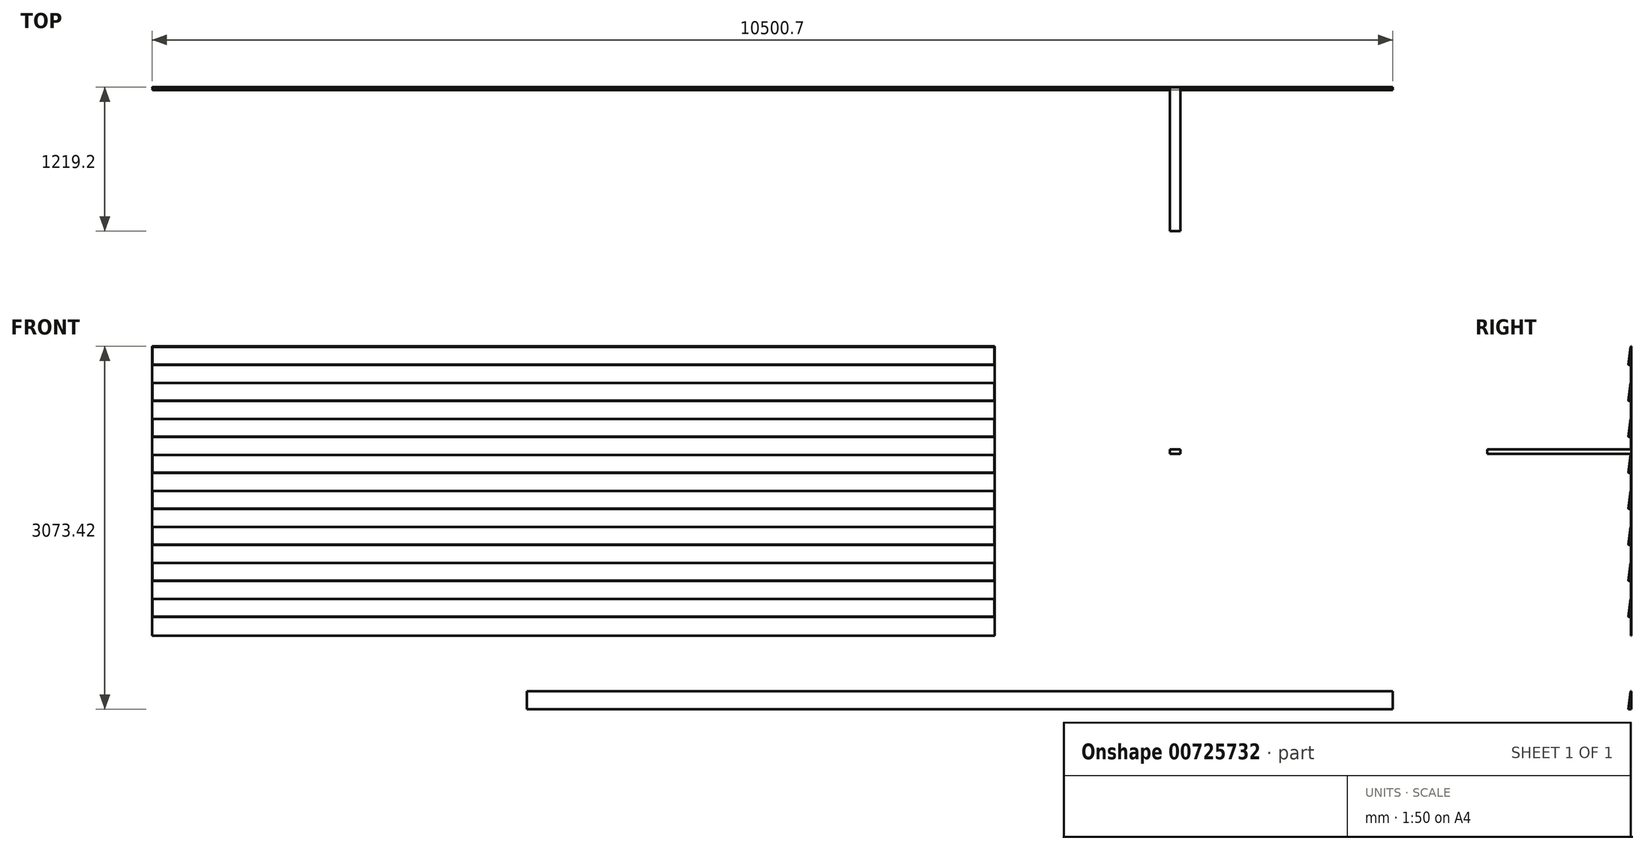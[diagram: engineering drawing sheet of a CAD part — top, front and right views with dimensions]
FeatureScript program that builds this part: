
annotation { "Feature Type Name" : "Feature", "Feature Type Description" : "" }
export const myFeature = defineFeature(function(context is Context, id is Id, definition is map)
    precondition{}
    {
        {
            var Q0;
            Q0=qCreatedBy(makeId("Front.planeOp"),FACE);
            var sketch = newSketch(context, id + "F0", { "sketchPlane" : qUnion([Q0])});
            skLineSegment(sketch, "E0.bottom", {"start": v(3562.35, -1219.2) * mm, "end": v(-3562.35, -1219.2) * mm});
            skLineSegment(sketch, "E0.top", {"start": v(3562.35, 1219.2) * mm, "end": v(-3562.35, 1219.2) * mm});
            skLineSegment(sketch, "E0.left", {"start": v(3562.35, -1219.2) * mm, "end": v(3562.35, 1219.2) * mm});
            skLineSegment(sketch, "E0.right", {"start": v(-3562.35, -1219.2) * mm, "end": v(-3562.35, 1219.2) * mm});
            skPoint(sketch, "E0.middle", {"position": v(0, 0) * mm});
            skLineSegment(sketch, "E1", {"start": v(-3562.35, -1066.8) * mm, "end": v(3562.35, -1066.8) * mm});
            skLineSegment(sketch, "E2", {"start": v(-3562.35, -914.4) * mm, "end": v(3562.35, -914.4) * mm});
            skLineSegment(sketch, "E3", {"start": v(-3562.35, -762) * mm, "end": v(3562.35, -762) * mm});
            skLineSegment(sketch, "E4", {"start": v(-3562.35, -609.6) * mm, "end": v(3562.35, -609.6) * mm});
            skLineSegment(sketch, "E5", {"start": v(-3562.35, -457.2) * mm, "end": v(3562.35, -457.2) * mm});
            skLineSegment(sketch, "E6", {"start": v(-3562.35, 0) * mm, "end": v(3562.35, 0) * mm});
            skLineSegment(sketch, "E7", {"start": v(-3562.35, -304.8) * mm, "end": v(3562.35, -304.8) * mm});
            skLineSegment(sketch, "E8", {"start": v(-3562.35, -152.4) * mm, "end": v(3562.35, -152.4) * mm});
            skLineSegment(sketch, "E9", {"start": v(-3562.35, 152.4) * mm, "end": v(3562.35, 152.4) * mm});
            skLineSegment(sketch, "E10", {"start": v(-3562.35, 457.2) * mm, "end": v(3562.35, 457.2) * mm});
            skLineSegment(sketch, "E11", {"start": v(-3562.35, 762) * mm, "end": v(3562.35, 762) * mm});
            skLineSegment(sketch, "E12", {"start": v(-3562.35, 304.8) * mm, "end": v(3562.35, 304.8) * mm});
            skLineSegment(sketch, "E13", {"start": v(-3562.35, 914.4) * mm, "end": v(3562.35, 914.4) * mm});
            skLineSegment(sketch, "E14", {"start": v(-3562.35, 609.6) * mm, "end": v(3562.35, 609.6) * mm});
            skLineSegment(sketch, "E15", {"start": v(-3562.35, 1066.8) * mm, "end": v(3562.35, 1066.8) * mm});
            skLineSegment(sketch, "E16.bottom", {"start": v(5137.26, 315.43) * mm, "end": v(5048.36, 315.43) * mm});
            skLineSegment(sketch, "E16.top", {"start": v(5137.26, 353.53) * mm, "end": v(5048.36, 353.53) * mm});
            skLineSegment(sketch, "E16.left", {"start": v(5137.26, 315.43) * mm, "end": v(5137.26, 353.53) * mm});
            skLineSegment(sketch, "E16.right", {"start": v(5048.36, 315.43) * mm, "end": v(5048.36, 353.53) * mm});
            skPoint(sketch, "E16.middle", {"position": v(5092.8, 334.48) * mm});
            skSolve(sketch);
        }
        {
            var Q0;
            Q0=qCreatedBy(makeId("Front.planeOp"),FACE);
            var sketch = newSketch(context, id + "F1", { "sketchPlane" : qUnion([Q0])});
            skLineSegment(sketch, "E17.bottom", {"start": v(-3565.53, -1225.55) * mm, "end": v(3565.53, -1225.55) * mm});
            skLineSegment(sketch, "E17.top", {"start": v(-3565.53, 1225.55) * mm, "end": v(3565.53, 1225.55) * mm});
            skLineSegment(sketch, "E17.left", {"start": v(-3565.53, -1225.55) * mm, "end": v(-3565.53, 1225.55) * mm});
            skLineSegment(sketch, "E17.right", {"start": v(3565.53, -1225.55) * mm, "end": v(3565.53, 1225.55) * mm});
            skPoint(sketch, "E17.middle", {"position": v(0, 0) * mm});
            skLineSegment(sketch, "E18.bottom", {"start": v(6935.14, -1695.47) * mm, "end": v(-392.76, -1695.47) * mm});
            skLineSegment(sketch, "E18.top", {"start": v(6935.14, -1847.87) * mm, "end": v(-392.76, -1847.87) * mm});
            skLineSegment(sketch, "E18.left", {"start": v(6935.14, -1695.47) * mm, "end": v(6935.14, -1847.87) * mm});
            skLineSegment(sketch, "E18.right", {"start": v(-392.76, -1695.47) * mm, "end": v(-392.76, -1847.87) * mm});
            skPoint(sketch, "E18.middle", {"position": v(3271.19, -1771.67) * mm});
            skSolve(sketch);
        }
        {
            var Q0;
            Q0=makeQuery(id+"F1.imprint","IMPRINT",FACE,{"disambiguationData":[TD([[makeQuery(id+"F1.imprint","IMPRINT",EDGE,{"derivedFrom":sQuery(id+"F1.wireOp",EDGE,"E17.bottom")}),1.0]])]});
            extrude(context, id + "F2", {"entities" : qUnion([Q0]), "depth" : 3.17 * mm, "offsetDistance" : 25.4 * mm});
        }
        {
            var Q0;
            {var subQ0=sQuery(id+"F0.wireOp",EDGE,"E11");Q0=makeQuery(id+"F0.imprint","IMPRINT",FACE,{"disambiguationData":[TD([[makeQuery(id+"F0.imprint","IMPRINT",EDGE,{"derivedFrom":subQ0}),1.0]])]});}
            var Q1;
            {var subQ0=sQuery(id+"F0.wireOp",EDGE,"E3");Q1=makeQuery(id+"F0.imprint","IMPRINT",FACE,{"disambiguationData":[TD([[makeQuery(id+"F0.imprint","IMPRINT",EDGE,{"derivedFrom":subQ0}),1.0]])]});}
            var Q2;
            {var subQ0=sQuery(id+"F0.wireOp",EDGE,"E1");Q2=makeQuery(id+"F0.imprint","IMPRINT",FACE,{"disambiguationData":[TD([[makeQuery(id+"F0.imprint","IMPRINT",EDGE,{"derivedFrom":subQ0}),1.0]])]});}
            var Q3;
            {var subQ0=sQuery(id+"F0.wireOp",EDGE,"E0.top");Q3=makeQuery(id+"F0.imprint","IMPRINT",FACE,{"disambiguationData":[TD([[makeQuery(id+"F0.imprint","IMPRINT",EDGE,{"derivedFrom":subQ0}),1.0]])]});}
            var Q4;
            {var subQ0=sQuery(id+"F0.wireOp",EDGE,"E10");Q4=makeQuery(id+"F0.imprint","IMPRINT",FACE,{"disambiguationData":[TD([[makeQuery(id+"F0.imprint","IMPRINT",EDGE,{"derivedFrom":subQ0}),1.0]])]});}
            var Q5;
            {var subQ0=sQuery(id+"F0.wireOp",EDGE,"E9");Q5=makeQuery(id+"F0.imprint","IMPRINT",FACE,{"disambiguationData":[TD([[makeQuery(id+"F0.imprint","IMPRINT",EDGE,{"derivedFrom":subQ0}),1.0]])]});}
            var Q6;
            {var subQ0=sQuery(id+"F0.wireOp",EDGE,"E5");Q6=makeQuery(id+"F0.imprint","IMPRINT",FACE,{"disambiguationData":[TD([[makeQuery(id+"F0.imprint","IMPRINT",EDGE,{"derivedFrom":subQ0}),1.0]])]});}
            var Q7;
            {var subQ0=sQuery(id+"F0.wireOp",EDGE,"E6");Q7=makeQuery(id+"F0.imprint","IMPRINT",FACE,{"disambiguationData":[TD([[makeQuery(id+"F0.imprint","IMPRINT",EDGE,{"derivedFrom":subQ0}),-1.0]])]});}
            extrude(context, id + "F3", {"entities" : qUnion([Q0, Q1, Q2, Q3, Q4, Q5, Q6, Q7]), "operationType" : NewBodyOperationType.ADD, "depth" : 25.4 * mm, "offsetDistance" : 25.4 * mm});
        }
        {
            var Q0;
            Q0=makeQuery(id+"F3.opExtrude","CAP_EDGE",EDGE,{"disambiguationData":[OSD([sQuery(id+"F0.wireOp",EDGE,"E13")])],"isStart":false});
            var Q1;
            Q1=makeQuery(id+"F3.opExtrude","CAP_EDGE",EDGE,{"disambiguationData":[OSD([sQuery(id+"F0.wireOp",EDGE,"E14")])],"isStart":false});
            var Q2;
            Q2=makeQuery(id+"F3.opExtrude","CAP_EDGE",EDGE,{"disambiguationData":[OSD([sQuery(id+"F0.wireOp",EDGE,"E12")])],"isStart":false});
            var Q3;
            Q3=makeQuery(id+"F3.opExtrude","CAP_EDGE",EDGE,{"disambiguationData":[OSD([sQuery(id+"F0.wireOp",EDGE,"E6")])],"isStart":false});
            var Q4;
            Q4=makeQuery(id+"F3.opExtrude","CAP_EDGE",EDGE,{"disambiguationData":[OSD([sQuery(id+"F0.wireOp",EDGE,"E7")])],"isStart":false});
            var Q5;
            Q5=makeQuery(id+"F3.opExtrude","CAP_EDGE",EDGE,{"disambiguationData":[OSD([sQuery(id+"F0.wireOp",EDGE,"E4")])],"isStart":false});
            var Q6;
            Q6=makeQuery(id+"F3.opExtrude","CAP_EDGE",EDGE,{"disambiguationData":[OSD([sQuery(id+"F0.wireOp",EDGE,"E2")])],"isStart":false});
            chamfer(context, id + "F4", {"entities" : qUnion([Q0, Q1, Q2, Q3, Q4, Q5, Q6]), "chamferType" : ChamferType.TWO_OFFSETS, "width1" : 152.4 * mm, "oppositeDirection" : true, "width2" : 19.05 * mm, "tangentPropagation" : true});
        }
        {
            var Q0;
            Q0=makeQuery(id+"F4.opChamfer","BLEND_EDGE",EDGE,{"blendedFrom":[makeQuery(id+"F3.opExtrude","CAP_EDGE",EDGE,{"disambiguationData":[OSD([sQuery(id+"F0.wireOp",EDGE,"E2")])],"isStart":false}),makeQuery(id+"F3.opExtrude","SWEPT_FACE",FACE,{"disambiguationData":[OSD([sQuery(id+"F0.wireOp",EDGE,"E1")])]})],"blendedInto":[makeQuery(id+"F3.opExtrude","SWEPT_FACE",FACE,{"disambiguationData":[OSD([sQuery(id+"F0.wireOp",EDGE,"E1")])]})]});
            var Q1;
            Q1=makeQuery(id+"F4.opChamfer","BLEND_EDGE",EDGE,{"blendedFrom":[makeQuery(id+"F3.opExtrude","CAP_EDGE",EDGE,{"disambiguationData":[OSD([sQuery(id+"F0.wireOp",EDGE,"E4")])],"isStart":false}),makeQuery(id+"F3.opExtrude","SWEPT_FACE",FACE,{"disambiguationData":[OSD([sQuery(id+"F0.wireOp",EDGE,"E3")])]})],"blendedInto":[makeQuery(id+"F3.opExtrude","SWEPT_FACE",FACE,{"disambiguationData":[OSD([sQuery(id+"F0.wireOp",EDGE,"E3")])]})]});
            var Q2;
            Q2=makeQuery(id+"F4.opChamfer","BLEND_EDGE",EDGE,{"blendedFrom":[makeQuery(id+"F3.opExtrude","CAP_EDGE",EDGE,{"disambiguationData":[OSD([sQuery(id+"F0.wireOp",EDGE,"E7")])],"isStart":false}),makeQuery(id+"F3.opExtrude","SWEPT_FACE",FACE,{"disambiguationData":[OSD([sQuery(id+"F0.wireOp",EDGE,"E5")])]})],"blendedInto":[makeQuery(id+"F3.opExtrude","SWEPT_FACE",FACE,{"disambiguationData":[OSD([sQuery(id+"F0.wireOp",EDGE,"E5")])]})]});
            var Q3;
            Q3=makeQuery(id+"F4.opChamfer","BLEND_EDGE",EDGE,{"blendedFrom":[makeQuery(id+"F3.opExtrude","CAP_EDGE",EDGE,{"disambiguationData":[OSD([sQuery(id+"F0.wireOp",EDGE,"E6")])],"isStart":false}),makeQuery(id+"F3.opExtrude","SWEPT_FACE",FACE,{"disambiguationData":[OSD([sQuery(id+"F0.wireOp",EDGE,"E8")])]})],"blendedInto":[makeQuery(id+"F3.opExtrude","SWEPT_FACE",FACE,{"disambiguationData":[OSD([sQuery(id+"F0.wireOp",EDGE,"E8")])]})]});
            var Q4;
            Q4=makeQuery(id+"F4.opChamfer","BLEND_EDGE",EDGE,{"blendedFrom":[makeQuery(id+"F3.opExtrude","CAP_EDGE",EDGE,{"disambiguationData":[OSD([sQuery(id+"F0.wireOp",EDGE,"E12")])],"isStart":false}),makeQuery(id+"F3.opExtrude","SWEPT_FACE",FACE,{"disambiguationData":[OSD([sQuery(id+"F0.wireOp",EDGE,"E9")])]})],"blendedInto":[makeQuery(id+"F3.opExtrude","SWEPT_FACE",FACE,{"disambiguationData":[OSD([sQuery(id+"F0.wireOp",EDGE,"E9")])]})]});
            var Q5;
            Q5=makeQuery(id+"F4.opChamfer","BLEND_EDGE",EDGE,{"blendedFrom":[makeQuery(id+"F3.opExtrude","CAP_EDGE",EDGE,{"disambiguationData":[OSD([sQuery(id+"F0.wireOp",EDGE,"E14")])],"isStart":false}),makeQuery(id+"F3.opExtrude","SWEPT_FACE",FACE,{"disambiguationData":[OSD([sQuery(id+"F0.wireOp",EDGE,"E10")])]})],"blendedInto":[makeQuery(id+"F3.opExtrude","SWEPT_FACE",FACE,{"disambiguationData":[OSD([sQuery(id+"F0.wireOp",EDGE,"E10")])]})]});
            var Q6;
            Q6=makeQuery(id+"F4.opChamfer","BLEND_EDGE",EDGE,{"blendedFrom":[makeQuery(id+"F3.opExtrude","CAP_EDGE",EDGE,{"disambiguationData":[OSD([sQuery(id+"F0.wireOp",EDGE,"E13")])],"isStart":false}),makeQuery(id+"F3.opExtrude","SWEPT_FACE",FACE,{"disambiguationData":[OSD([sQuery(id+"F0.wireOp",EDGE,"E11")])]})],"blendedInto":[makeQuery(id+"F3.opExtrude","SWEPT_FACE",FACE,{"disambiguationData":[OSD([sQuery(id+"F0.wireOp",EDGE,"E11")])]})]});
            var Q7;
            Q7=makeQuery(id+"F3.opExtrude","CAP_EDGE",EDGE,{"disambiguationData":[OSD([sQuery(id+"F0.wireOp",EDGE,"E15")])],"isStart":false});
            chamfer(context, id + "F5", {"entities" : qUnion([Q0, Q1, Q2, Q3, Q4, Q5, Q6, Q7]), "width" : 3.17 * mm, "tangentPropagation" : true});
        }
        {
            var Q0;
            Q0=makeQuery(id+"F3.opExtrude","CAP_EDGE",EDGE,{"disambiguationData":[OSD([sQuery(id+"F0.wireOp",EDGE,"E0.top")])],"isStart":false});
            chamfer(context, id + "F6", {"entities" : qUnion([Q0]), "chamferType" : ChamferType.TWO_OFFSETS, "width1" : 152.4 * mm, "oppositeDirection" : false, "width2" : 19.05 * mm, "tangentPropagation" : true});
        }
        {
            var Q0;
            Q0=makeQuery(id+"F1.imprint","IMPRINT",FACE,{"disambiguationData":[TD([[makeQuery(id+"F1.imprint","IMPRINT",EDGE,{"derivedFrom":sQuery(id+"F1.wireOp",EDGE,"E18.bottom")}),1.0]])]});
            extrude(context, id + "F7", {"entities" : qUnion([Q0]), "depth" : 25.4 * mm, "offsetDistance" : 25.4 * mm});
        }
        {
            var Q0;
            Q0=makeQuery(id+"F7.opExtrude","CAP_EDGE",EDGE,{"disambiguationData":[OSD([sQuery(id+"F1.wireOp",EDGE,"E18.bottom")])],"isStart":false});
            chamfer(context, id + "F8", {"entities" : qUnion([Q0]), "chamferType" : ChamferType.TWO_OFFSETS, "width1" : 152.4 * mm, "oppositeDirection" : false, "width2" : 19.05 * mm, "tangentPropagation" : true});
        }
        {
            var Q0;
            Q0=makeQuery(id+"F0.imprint","IMPRINT",FACE,{"disambiguationData":[TD([[makeQuery(id+"F0.imprint","IMPRINT",EDGE,{"derivedFrom":sQuery(id+"F0.wireOp",EDGE,"E16.bottom")}),-1.0]])]});
            extrude(context, id + "F9", {"entities" : qUnion([Q0]), "depth" : 1219.2 * mm, "offsetDistance" : 25.4 * mm});
        }
    });
